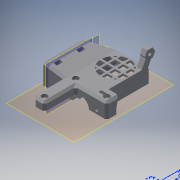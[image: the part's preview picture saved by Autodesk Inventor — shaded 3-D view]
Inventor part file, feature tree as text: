
AUTODESK INVENTOR PART (.ipt)
format: ipt  version: 2018 (Build 220112000, 112)  size: 836,608 bytes
history: native  units: mm
features: sketch x24, extrude x23, reference x23, other x7, plane x4, projected_geometry x3, mirror x2, chamfer x2, revolve x1, loft x1, split x1
ambient origin geometry x8: Origin, YZ Plane, XZ Plane, XY Plane, X Axis, Y Axis, Z Axis, Center Point
bodies: Solid1 (feature_tree), Solid2 (feature_tree), Solid3 (feature_tree)
feature tree (91):
  sketch  "Sketch2"  dims[d3=13.25mm d4=0.0mm d5=3.0mm]
  plane  "Work Plane3"
  extrude  "Extrusion1"  Depth=3.0mm
  revolve  "Revolution1"  Angle=90.0deg
  mirror  "Mirror1"
  extrude  "Extrusion2"  Depth=0.2mm
  extrude  "Extrusion3"  Depth=0.2mm
  extrude  "Extrusion4"  Depth=0.2mm
  extrude  "Extrusion5"  Depth=3.0mm
  extrude  "Extrusion6"  Depth=6.0mm TaperAngle=0.0deg
  extrude  "Extrusion7"  Depth=10.0mm
  mirror  "Mirror2"
  extrude  "Extrusion8"  Depth=2.0mm TaperAngle=0.0deg
  extrude  "Extrusion9"  Depth=3.5mm
  extrude  "Extrusion10"  Depth=3.5mm
  extrude  "Extrusion11"  Depth=5.8mm
  extrude  "Extrusion12"  Depth=2.8mm TaperAngle=0.0deg
  extrude  "Extrusion13"  Depth=0.2mm
  extrude  "Extrusion14"  Depth=1.0mm TaperAngle=0.0deg
  extrude  "Extrusion15"  Depth=0.5mm
  extrude  "Extrusion16"  Depth=10.0mm
  extrude  "Extrusion17"  Depth=3.2mm
  sketch  "Sketch24"  dims[d81=8.0mm d82=0.0mm d83=6.3mm]
  plane  "Work Plane4"
  loft  "Loft1"
  extrude  "Extrusion18"  Depth=6.0mm
  plane  "Work Plane5"
  extrude  "Extrusion19"  Depth=5.0mm TaperAngle=0.0deg
  chamfer  "Chamfer1"  Distance=5.0mm
  extrude  "Extrusion20"  Depth=3.2mm TaperAngle=0.0deg
  extrude  "Extrusion21"  Depth=15.0mm
  chamfer  "Chamfer2"  Distance=40.0mm
  plane  "Work Plane6"
  split  "Split1"
  reference  "Reference5"
  reference  "Reference6"
  reference  "Reference7"
  sketch  "Sketch4"  dims[d6=1.5mm d19=90.0deg]
  reference  "Reference15"
  reference  "Reference16"
  reference  "Reference17"
  sketch  "Sketch5"  dims[d20=0.2mm d21=0.2mm]
  reference  "Reference19"
  reference  "Reference20"
  reference  "Reference21"
  reference  "Reference22"
  sketch  "Sketch6"  dims[d22=0.2mm d23=0.2mm]
  reference  "Reference23"
  sketch  "Sketch7"  dims[d24=0.2mm d25=0.2mm]
  sketch  "Sketch8"  dims[d26=0.2mm d27=3.0mm]
  sketch  "Sketch10"  dims[d28=6.0mm d29=0.0mm d30=6.0mm d31=0.0mm]
  projected_geometry  "Projected Loop2"
  projected_geometry  "Projected Loop3"
  sketch  "Sketch11"  dims[d32=20.0mm d34=8.0mm d35=10.0mm d37=10.0mm d39=20.0mm d41=8.0mm d42=10.0mm d44=10.0mm]
  reference  "Reference25"
  sketch  "Sketch12"  dims[d46=2.0mm d47=2.0mm d48=0.0mm]
  projected_geometry  "Projected Loop4"
  sketch  "Sketch14"  dims[d49=22.0mm d50=0.0mm d55=3.5mm]
  sketch  "Sketch15"  dims[d56=3.2mm d57=3.5mm]
  reference  "Reference28"
  sketch  "Sketch16"  dims[d58=8.0mm d59=0.0mm d60=5.8mm]
  reference  "Reference29"
  reference  "Reference30"
  sketch  "Sketch17"  dims[d61=2.8mm d62=0.0mm d64=2.8mm d65=0.0mm]
  reference  "Reference31"
  reference  "Reference32"
  sketch  "Sketch18"  dims[d66=2.8mm d67=0.0mm d68=0.2mm]
  reference  "Reference33"
  sketch  "Sketch19"  dims[d69=3.0mm d70=0.0mm d72=1.0mm d73=0.0mm]
  sketch  "Sketch20"  dims[d74=0.5mm d75=0.5mm]
  reference  "Reference34"
  sketch  "Sketch21"  dims[d76=0.5mm d77=10.0mm]
  sketch  "Sketch22"  dims[d78=8.0mm d79=0.0mm d80=3.2mm]
  sketch  "Sketch25"  dims[d84=3.2mm d85=0.0mm d86=6.0mm]
  reference  "Reference35"
  reference  "Reference36"
  sketch  "Sketch26"  dims[d87=9.0mm d88=5.0mm d89=0.0mm]
  reference  "Reference37"
  reference  "Reference38"
  sketch  "Sketch28"  dims[d90=3.2mm d91=5.0mm d92=0.0mm]
  sketch  "Sketch29"  dims[d93=6.2mm d94=3.2mm d95=0.0mm]
  sketch  "Sketch30"  dims[d96=20.0mm d97=42.0mm d98=40.0mm d99=0.0mm d100=90.0deg d101=0.0mm d102=90.0deg d103=15.0mm d104=0.0mm d106=-4.5mm d107=6.0mm d108=6.0mm d109=13.0mm d110=3.0mm d111=0.0mm d112=2.0mm d113=2.0mm d114=45.0deg d115=5.7mm d116=3.0mm d117=0.0mm d118=5.7mm d119=3.0mm d120=0.0mm d121=2.0mm d122=2.0mm d123=45.0deg]
  parser-record x1  (decoder bookkeeping rows leaked as tree rows — omitted from the tree; the rows remain in map.json)
  extrude  "Extruder Head.iam"  TaperAngle=0.0deg  [1 undecoded]
  other  "NEMA17:1"
  extrude  "Extruder:1"  TaperAngle=0.0deg  [1 undecoded]
  other  "30mm Fan:1"
  other  "30mm Fan Case"
  other  "Radial-Cooling-Fan-5015-DC12V:1"
  other  "top:3"
  other  "x-carriage-with-endstop-trigger:1"
note: 2 required parameter values undecoded (feature->parameter linkage not recoverable at this tier; creation-order binding heuristic only, values carry confidence <= 0.55)
note: 1 file-system path scrubbed to <path> (originals preserved in map.json)
